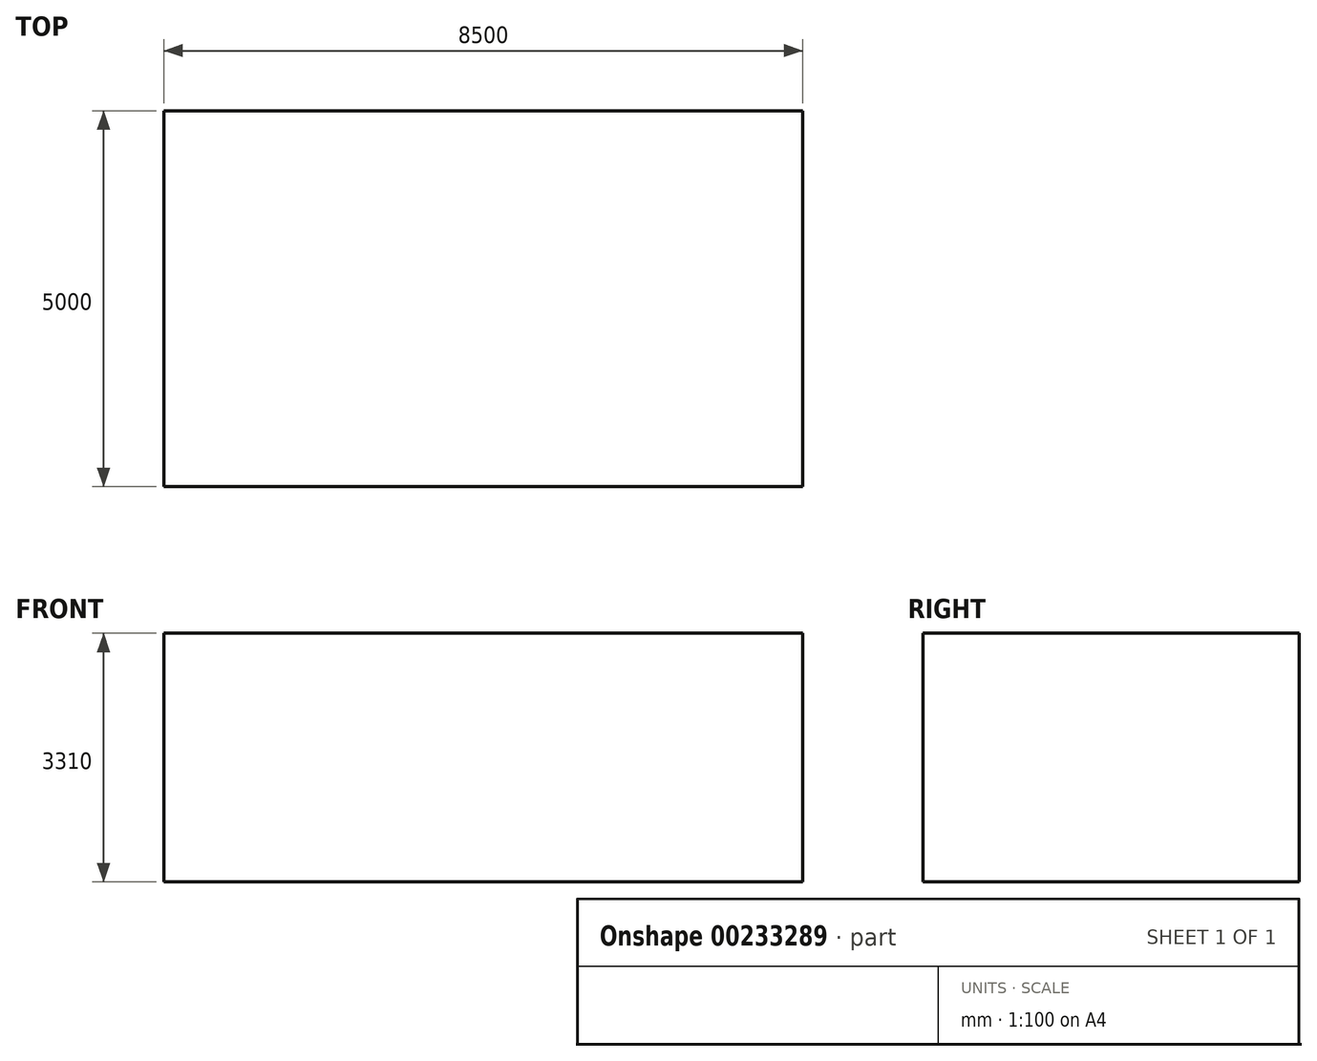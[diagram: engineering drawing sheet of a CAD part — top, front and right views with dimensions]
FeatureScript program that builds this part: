
annotation { "Feature Type Name" : "Feature", "Feature Type Description" : "" }
export const myFeature = defineFeature(function(context is Context, id is Id, definition is map)
    precondition{}
    {
        {
            var Q0;
            Q0=qCreatedBy(makeId("Front.planeOp"),FACE);
            var sketch = newSketch(context, id + "F0", { "sketchPlane" : qUnion([Q0])});
            skLineSegment(sketch, "E0.bottom", {"start": v(-2803.48, 1660.75) * mm, "end": v(5696.52, 1660.75) * mm});
            skLineSegment(sketch, "E0.top", {"start": v(-2803.48, -1649.25) * mm, "end": v(5696.52, -1649.25) * mm});
            skLineSegment(sketch, "E0.left", {"start": v(-2803.48, 1660.75) * mm, "end": v(-2803.48, -1649.25) * mm});
            skLineSegment(sketch, "E0.right", {"start": v(5696.52, 1660.75) * mm, "end": v(5696.52, -1649.25) * mm});
            skSolve(sketch);
        }
        {
            var Q0;
            Q0=makeQuery(id+"F0.imprint","IMPRINT",FACE,{"disambiguationData":[TD([[makeQuery(id+"F0.imprint","IMPRINT",EDGE,{"derivedFrom":sQuery(id+"F0.wireOp",EDGE,"E0.bottom")}),-1.0]])]});
            extrude(context, id + "F1", {"entities" : qUnion([Q0]), "depth" : 5000 * mm});
        }
    });
